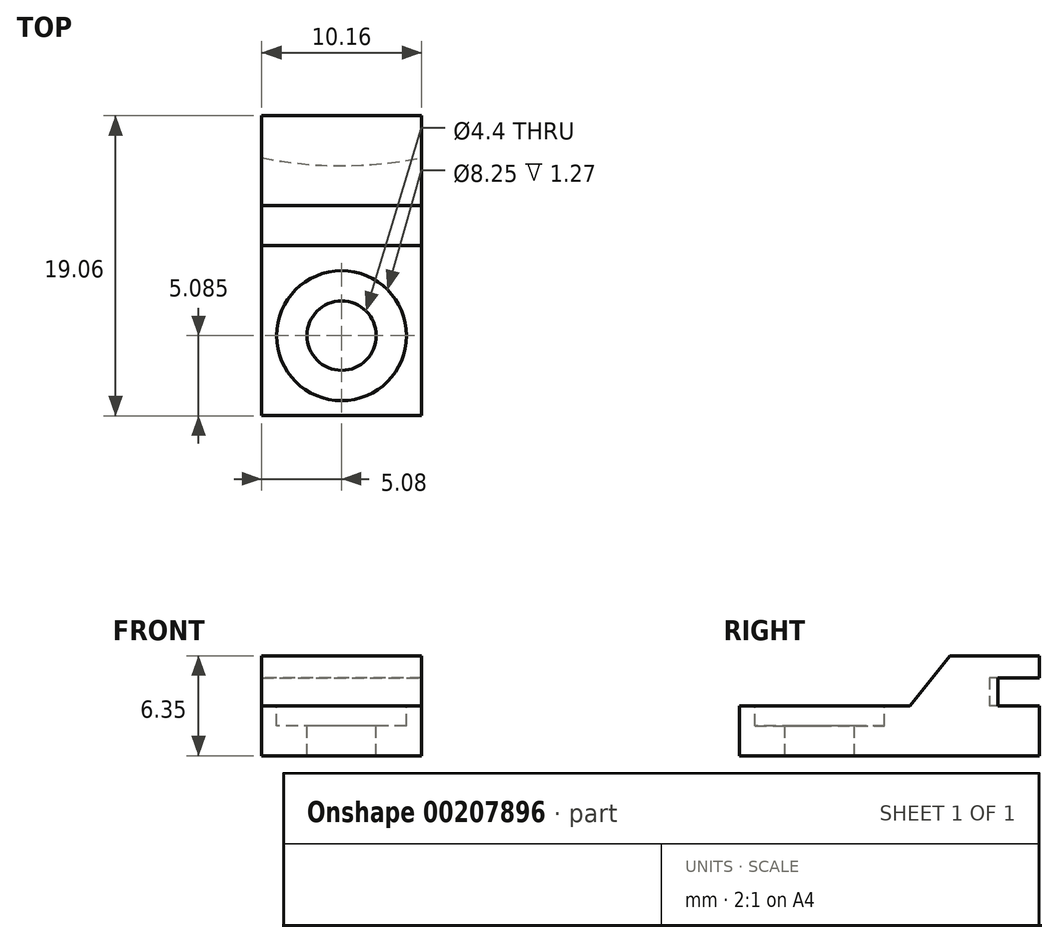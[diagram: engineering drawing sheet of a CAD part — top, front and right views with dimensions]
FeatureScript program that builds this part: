
annotation { "Feature Type Name" : "Feature", "Feature Type Description" : "" }
export const myFeature = defineFeature(function(context is Context, id is Id, definition is map)
    precondition{}
    {
        {
            var Q0;
            Q0=qCreatedBy(makeId("Top.planeOp"),FACE);
            var sketch = newSketch(context, id + "F0", { "sketchPlane" : qUnion([Q0])});
            skLineSegment(sketch, "E0.bottom", {"start": v(5.08, -9.53) * mm, "end": v(-5.08, -9.53) * mm});
            skLineSegment(sketch, "E0.top", {"start": v(5.08, 9.53) * mm, "end": v(-5.08, 9.53) * mm});
            skLineSegment(sketch, "E0.left", {"start": v(5.08, -9.52) * mm, "end": v(5.08, 9.53) * mm});
            skLineSegment(sketch, "E0.right", {"start": v(-5.08, -9.53) * mm, "end": v(-5.08, 9.52) * mm});
            skPoint(sketch, "E0.middle", {"position": v(0, 0) * mm});
            skSolve(sketch);
        }
        {
            var Q0;
            Q0 = qSketchRegion(id + "F0", true);
            extrude(context, id + "F1", {"entities" : qUnion([Q0]), "depth" : 3.17 * mm});
        }
        {
            var Q0;
            Q0=makeQuery(id+"F1.opExtrude","SWEPT_FACE",FACE,{"disambiguationData":[OSD([sQuery(id+"F0.wireOp",EDGE,"E0.left")])]});
            var sketch = newSketch(context, id + "F2", { "sketchPlane" : qUnion([Q0])});
            skLineSegment(sketch, "E1", {"start": v(1.27, 3.18) * mm, "end": v(3.81, 6.35) * mm});
            skLineSegment(sketch, "E2", {"start": v(3.81, 6.35) * mm, "end": v(9.53, 6.35) * mm});
            skLineSegment(sketch, "E3", {"start": v(9.53, 6.35) * mm, "end": v(9.53, 3.18) * mm});
            skLineSegment(sketch, "E4", {"start": v(9.53, 3.17) * mm, "end": v(1.27, 3.17) * mm});
            skSolve(sketch);
        }
        {
            var Q0;
            Q0=makeQuery(id+"F2.imprint","IMPRINT",FACE,{"disambiguationData":[TD([[makeQuery(id+"F2.imprint","IMPRINT",EDGE,{"derivedFrom":sQuery(id+"F2.wireOp",EDGE,"E1")}),-1.0]])]});
            var sketch = newSketch(context, id + "F3", { "sketchPlane" : qUnion([Q0])});
            skSolve(sketch);
        }
        {
            var Q0;
            Q0=makeQuery(id+"F2.imprint","IMPRINT",FACE,{"disambiguationData":[TD([[makeQuery(id+"F2.imprint","IMPRINT",EDGE,{"derivedFrom":sQuery(id+"F2.wireOp",EDGE,"E1")}),-1.0]])]});
            var Q1;
            Q1=makeQuery(id+"F1.opExtrude","SWEPT_FACE",FACE,{"disambiguationData":[OSD([sQuery(id+"F0.wireOp",EDGE,"E0.right")])]});
            extrude(context, id + "F4", {"entities" : qUnion([Q0]), "operationType" : NewBodyOperationType.ADD, "endBound" : BoundingType.UP_TO_SURFACE, "oppositeDirection" : true, "endBoundEntityFace" : qUnion([Q1]), "depth" : 25.4 * mm});
        }
        {
            var Q0;
            Q0=makeQuery(id+"F1.opExtrude","CAP_FACE",FACE,{"disambiguationData":[OSD([sQuery(id+"F0.wireOp",EDGE,"E0.bottom"),sQuery(id+"F0.wireOp",EDGE,"E0.top"),sQuery(id+"F0.wireOp",EDGE,"E0.left"),sQuery(id+"F0.wireOp",EDGE,"E0.right")])],"isStart":false});
            var sketch = newSketch(context, id + "F5", { "sketchPlane" : qUnion([Q0])});
            skPoint(sketch, "E5", {"position": v(0, -4.45) * mm});
            skSolve(sketch);
        }
        {
            var Q0;
            Q0=sQuery(id+"F5.wireOp",VERTEX,"E5");
            var Q1;
            Q1=makeQuery(id+"F1.opExtrude","SWEPT_BODY",BODY,{"disambiguationData":[OSD([sQuery(id+"F0.wireOp",EDGE,"E0.bottom"),sQuery(id+"F0.wireOp",EDGE,"E0.top"),sQuery(id+"F0.wireOp",EDGE,"E0.left"),sQuery(id+"F0.wireOp",EDGE,"E0.right")])]});
            hole(context, id + "F6", {"style" : HoleStyle.C_BORE, "endStyle" : HoleEndStyle.BLIND, "holeDiameter" : 4.4 * mm, "cBoreDiameter" : 8.25 * mm, "cBoreDepth" : 1.27 * mm, "holeDepth" : 12.7 * mm, "startFromSketch" : true, "locations" : qUnion([Q0]), "scope" : qUnion([Q1])});
        }
        {
            var Q0;
            Q0=makeQuery(id+"F1.opExtrude","CAP_FACE",FACE,{"disambiguationData":[OSD([sQuery(id+"F0.wireOp",EDGE,"E0.bottom"),sQuery(id+"F0.wireOp",EDGE,"E0.top"),sQuery(id+"F0.wireOp",EDGE,"E0.left"),sQuery(id+"F0.wireOp",EDGE,"E0.right")])],"isStart":false});
            var sketch = newSketch(context, id + "F7", { "sketchPlane" : qUnion([Q0])});
            skCircle(sketch, "E6", {"center": v(0, 31.75) * mm, "radius": 25.4 * mm});
            skSolve(sketch);
        }
        {
            var Q0;
            Q0=makeQuery(id+"F7.imprint","IMPRINT",FACE,{"disambiguationData":[TD([[makeQuery(id+"F7.imprint","IMPRINT",EDGE,{"derivedFrom":sQuery(id+"F7.wireOp",EDGE,"E6")}),1.0]])]});
            extrude(context, id + "F8", {"entities" : qUnion([Q0]), "operationType" : NewBodyOperationType.REMOVE, "depth" : 1.78 * mm});
        }
    });
